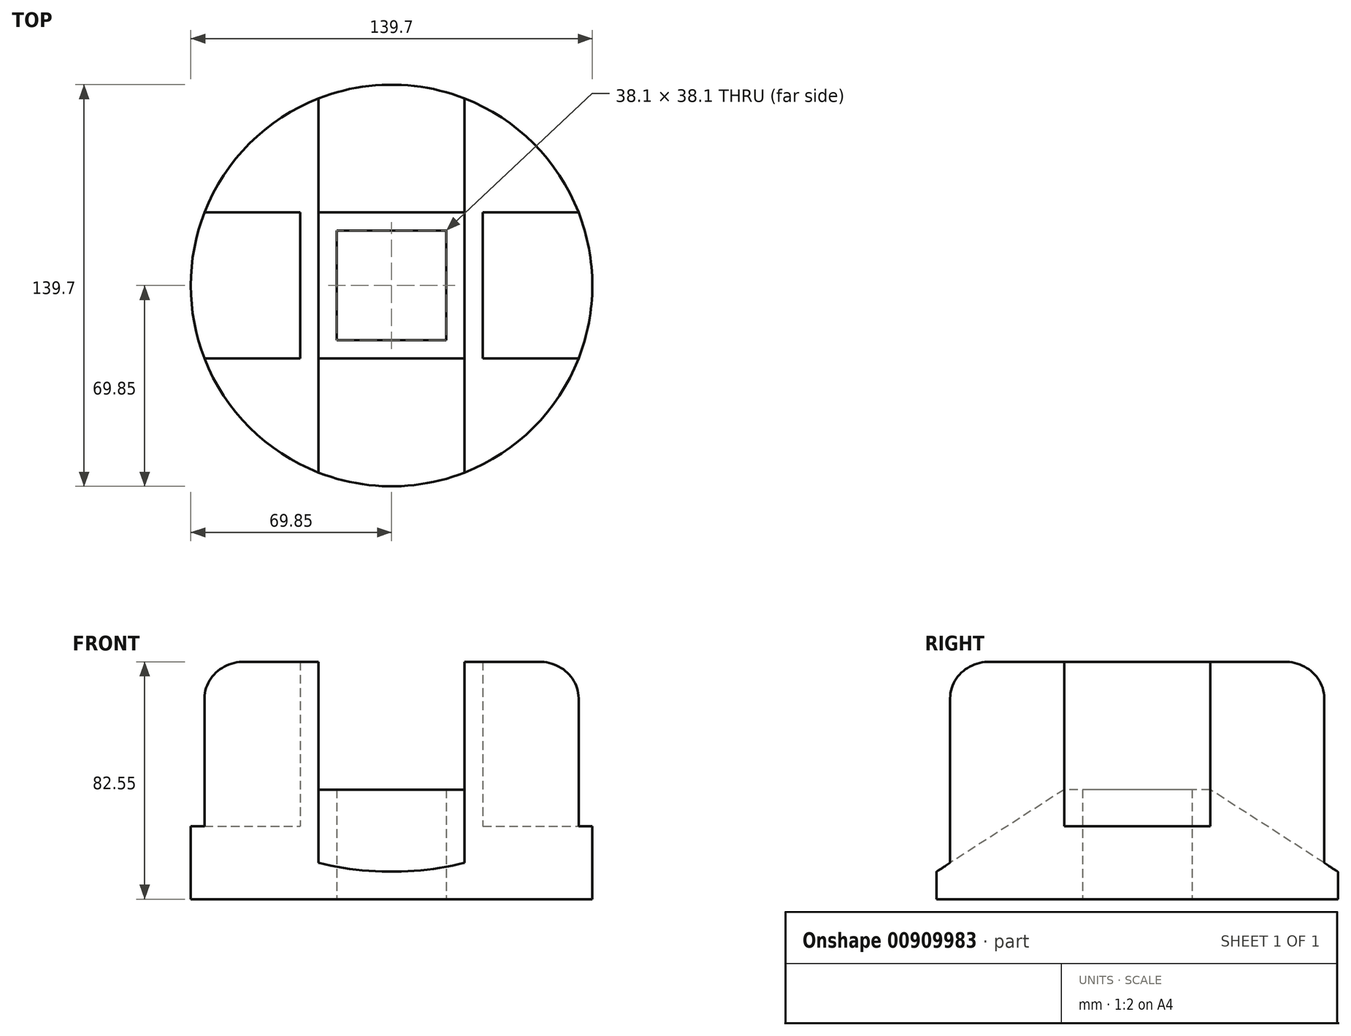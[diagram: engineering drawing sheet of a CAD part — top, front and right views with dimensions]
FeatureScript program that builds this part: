
annotation { "Feature Type Name" : "Feature", "Feature Type Description" : "" }
export const myFeature = defineFeature(function(context is Context, id is Id, definition is map)
    precondition{}
    {
        {
            var Q0;
            Q0=qCreatedBy(makeId("Front.planeOp"),FACE);
            var sketch = newSketch(context, id + "F0", { "sketchPlane" : qUnion([Q0])});
            skLineSegment(sketch, "E0", {"start": v(34.92, -432) * mm, "end": v(34.92, -381.2) * mm});
            skLineSegment(sketch, "E1", {"start": v(0, 0) * mm, "end": v(69.85, 0) * mm});
            skLineSegment(sketch, "E2", {"start": v(69.85, 0) * mm, "end": v(69.85, 69.85) * mm});
            skLineSegment(sketch, "E3", {"start": v(57.15, 82.55) * mm, "end": v(0, 82.55) * mm});
            skLineSegment(sketch, "E4", {"start": v(0, 82.55) * mm, "end": v(0, 0) * mm});
            skLineSegment(sketch, "E5", {"start": v(31.75, 82.55) * mm, "end": v(31.75, 25.4) * mm});
            skLineSegment(sketch, "E6", {"start": v(31.75, 25.4) * mm, "end": v(69.85, 25.4) * mm});
            skPoint(sketch, "E7.visualSharp", {"position": v(69.85, 82.55) * mm});
            skArc(sketch, "E7.filletArc", {"start": v(69.85, 69.85) * mm, "mid": v(66.13, 78.83) * mm, "end": v(57.15, 82.55) * mm});
            skLineSegment(sketch, "E8.bottom", {"start": v(-69.85, 82.55) * mm, "end": v(-31.75, 82.55) * mm});
            skLineSegment(sketch, "E8.top", {"start": v(-69.85, 25.4) * mm, "end": v(-31.75, 25.4) * mm});
            skLineSegment(sketch, "E8.left", {"start": v(-69.85, 82.55) * mm, "end": v(-69.85, 25.4) * mm});
            skLineSegment(sketch, "E8.right", {"start": v(-31.75, 82.55) * mm, "end": v(-31.75, 25.4) * mm});
            skLineSegment(sketch, "E9", {"start": v(-31.75, 25.4) * mm, "end": v(31.75, 25.4) * mm, "construction": true});
            skLineSegment(sketch, "E10", {"start": v(0, 25.4) * mm, "end": v(0, 0) * mm, "construction": true});
            skLineSegment(sketch, "E11", {"start": v(22.23, -889) * mm, "end": v(0, -889) * mm});
            skLineSegment(sketch, "E12", {"start": v(34.93, -432) * mm, "end": v(28.58, -432) * mm});
            skLineSegment(sketch, "E13", {"start": v(28.58, -432) * mm, "end": v(28.58, -723.9) * mm});
            skLineSegment(sketch, "E14", {"start": v(28.58, -723.9) * mm, "end": v(22.23, -736.6) * mm});
            skLineSegment(sketch, "E15", {"start": v(22.23, -736.6) * mm, "end": v(22.23, -889) * mm});
            skLineSegment(sketch, "E16", {"start": v(34.93, -381.2) * mm, "end": v(38.1, -381.2) * mm});
            skLineSegment(sketch, "E17", {"start": v(38.1, -381.2) * mm, "end": v(38.1, 0) * mm});
            skLineSegment(sketch, "E18", {"start": v(0, 0) * mm, "end": v(0, -889) * mm});
            skSolve(sketch);
        }
        {
            var Q0;
            {var subQ0=sQuery(id+"F0.wireOp",EDGE,"E5");Q0=makeQuery(id+"F0.imprint","IMPRINT",FACE,{"disambiguationData":[TD([[makeQuery(id+"F0.imprint","IMPRINT",EDGE,{"derivedFrom":subQ0}),1.0]])]});}
            var Q1;
            {var subQ5=sQuery(id+"F0.wireOp",EDGE,"E4");Q1=makeQuery(id+"F0.imprint","IMPRINT",FACE,{"disambiguationData":[TD([[makeQuery(id+"F0.imprint","IMPRINT",EDGE,{"derivedFrom":subQ5}),1.0]])]});}
            var Q2;
            Q2=sQuery(id+"F0.wireOp",EDGE,"E4");
            revolve(context, id + "F1", {"surfaceOperationType" : NewSurfaceOperationType.NEW, "entities" : qUnion([Q0, Q1]), "axis" : qUnion([Q2]), "revolveType" : RevolveType.FULL});
        }
        {
            var Q0;
            {var subQ0=sQuery(id+"F0.wireOp",EDGE,"E5");Q0=makeQuery(id+"F0.imprint","IMPRINT",FACE,{"disambiguationData":[TD([[makeQuery(id+"F0.imprint","IMPRINT",EDGE,{"derivedFrom":subQ0}),1.0]])]});}
            var Q1;
            Q1=makeQuery(id+"F0.imprint","IMPRINT",FACE,{"disambiguationData":[TD([[makeQuery(id+"F0.imprint","IMPRINT",EDGE,{"derivedFrom":sQuery(id+"F0.wireOp",EDGE,"E8.bottom")}),-1.0]])]});
            extrude(context, id + "F2", {"entities" : qUnion([Q0, Q1]), "operationType" : NewBodyOperationType.REMOVE, "oppositeDirection" : true, "depth" : 50.8 * mm, "offsetDistance" : 25 * mm, "symmetric" : true});
        }
        {
            var Q0;
            Q0=qCreatedBy(makeId("Right.planeOp"),FACE);
            var sketch = newSketch(context, id + "F3", { "sketchPlane" : qUnion([Q0])});
            skLineSegment(sketch, "E19", {"start": v(69.85, 82.55) * mm, "end": v(69.85, 9.52) * mm});
            skLineSegment(sketch, "E20", {"start": v(69.85, 9.52) * mm, "end": v(25.4, 38.1) * mm});
            skLineSegment(sketch, "E21", {"start": v(25.4, 38.1) * mm, "end": v(-25.4, 38.1) * mm});
            skLineSegment(sketch, "E22", {"start": v(-25.4, 38.1) * mm, "end": v(-69.85, 9.52) * mm});
            skLineSegment(sketch, "E23", {"start": v(-69.85, 9.52) * mm, "end": v(-69.85, 82.55) * mm});
            skLineSegment(sketch, "E24", {"start": v(-69.85, 82.55) * mm, "end": v(69.85, 82.55) * mm});
            skLineSegment(sketch, "E25", {"start": v(0, 0) * mm, "end": v(0, 82.55) * mm, "construction": true});
            skSolve(sketch);
        }
        {
            var Q0;
            Q0=makeQuery(id+"F3.imprint","IMPRINT",FACE,{"disambiguationData":[TD([[makeQuery(id+"F3.imprint","IMPRINT",EDGE,{"derivedFrom":sQuery(id+"F3.wireOp",EDGE,"E19")}),-1.0]])]});
            extrude(context, id + "F4", {"entities" : qUnion([Q0]), "operationType" : NewBodyOperationType.REMOVE, "oppositeDirection" : true, "depth" : 50.8 * mm, "offsetDistance" : 25 * mm, "symmetric" : true});
        }
        {
            var Q0;
            Q0=makeQuery(id+"F1.opRevolve","SWEPT_FACE",FACE,{"disambiguationData":[OSD([sQuery(id+"F0.wireOp",EDGE,"E1")])]});
            var sketch = newSketch(context, id + "F5", { "sketchPlane" : qUnion([Q0])});
            skLineSegment(sketch, "E26.bottom", {"start": v(-19.05, 19.05) * mm, "end": v(19.05, 19.05) * mm});
            skLineSegment(sketch, "E26.top", {"start": v(-19.05, -19.05) * mm, "end": v(19.05, -19.05) * mm});
            skLineSegment(sketch, "E26.left", {"start": v(-19.05, 19.05) * mm, "end": v(-19.05, -19.05) * mm});
            skLineSegment(sketch, "E26.right", {"start": v(19.05, 19.05) * mm, "end": v(19.05, -19.05) * mm});
            skLineSegment(sketch, "E27", {"start": v(-19.05, 19.05) * mm, "end": v(19.05, -19.05) * mm, "construction": true});
            skLineSegment(sketch, "E28", {"start": v(19.05, 19.05) * mm, "end": v(-19.05, -19.05) * mm, "construction": true});
            skSolve(sketch);
        }
        {
            var Q0;
            Q0=makeQuery(id+"F5.imprint","IMPRINT",FACE,{"disambiguationData":[TD([[makeQuery(id+"F5.imprint","IMPRINT",EDGE,{"derivedFrom":sQuery(id+"F5.wireOp",EDGE,"E26.bottom")}),-1.0]])]});
            extrude(context, id + "F6", {"entities" : qUnion([Q0]), "operationType" : NewBodyOperationType.REMOVE, "endBound" : BoundingType.THROUGH_ALL, "oppositeDirection" : true, "depth" : 25 * mm, "offsetDistance" : 25 * mm});
        }
    });
